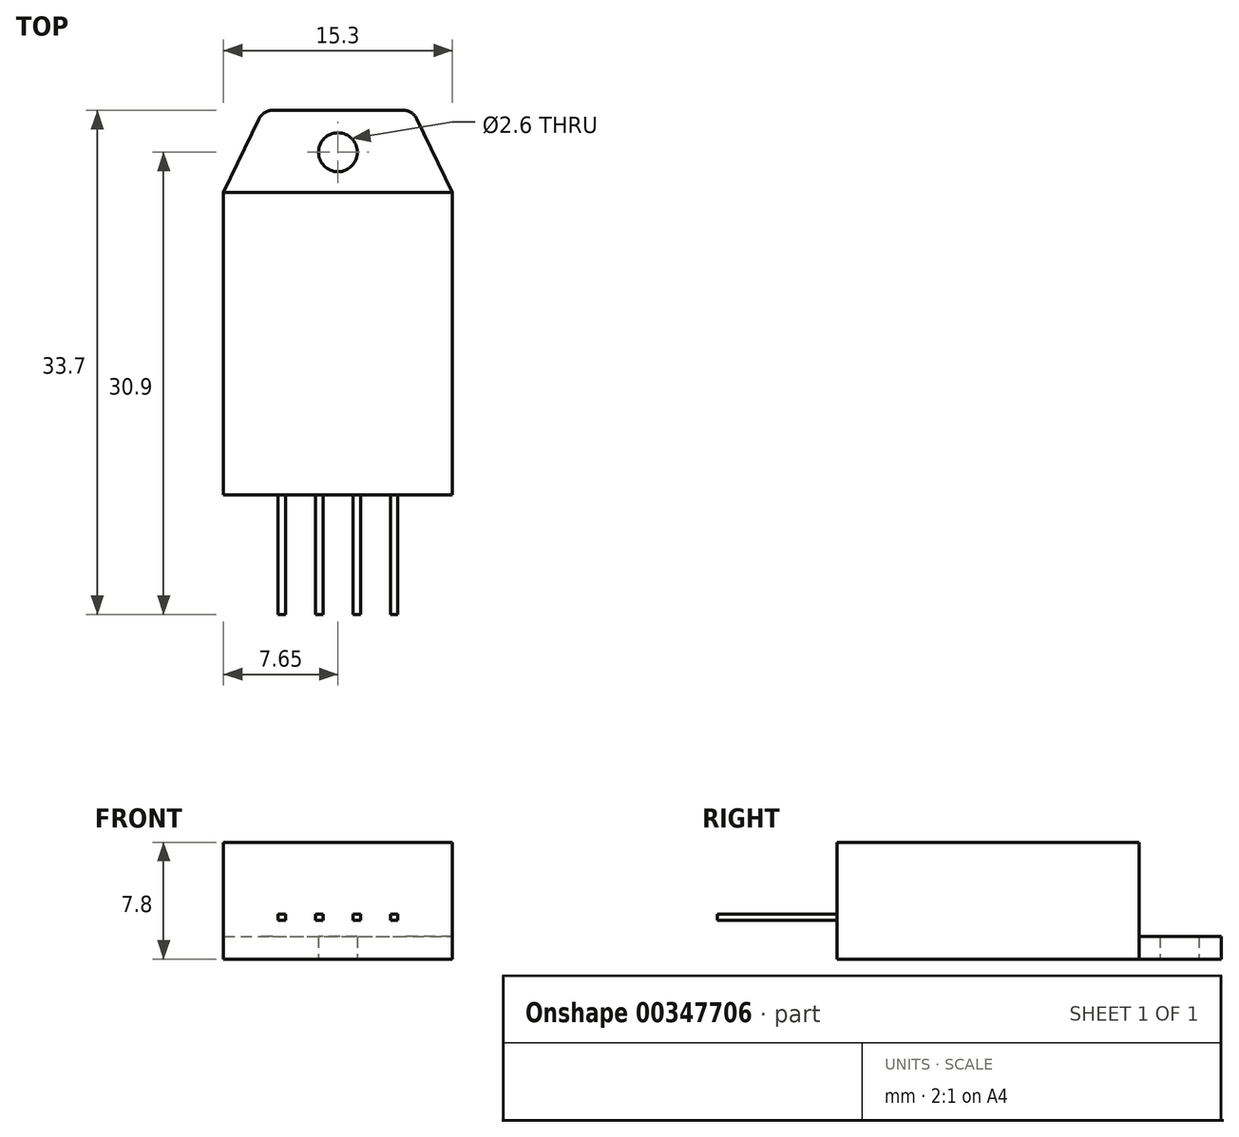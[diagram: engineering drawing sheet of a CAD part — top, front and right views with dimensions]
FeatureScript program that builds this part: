
annotation { "Feature Type Name" : "Feature", "Feature Type Description" : "" }
export const myFeature = defineFeature(function(context is Context, id is Id, definition is map)
    precondition{}
    {
        {
            var Q0;
            Q0=qCreatedBy(makeId("Top.planeOp"),FACE);
            var sketch = newSketch(context, id + "F0", { "sketchPlane" : qUnion([Q0])});
            skCircle(sketch, "E0", {"center": v(0, 0) * mm, "radius": 1.3 * mm});
            skLineSegment(sketch, "E1", {"start": v(-7.65, -22.9) * mm, "end": v(-7.65, -2.7) * mm});
            skLineSegment(sketch, "E2", {"start": v(-7.65, -2.7) * mm, "end": v(-5.27, 2.23) * mm});
            skLineSegment(sketch, "E3.MirrorCS", {"start": v(7.65, -2.7) * mm, "end": v(5.27, 2.23) * mm});
            skLineSegment(sketch, "E4.MirrorCS", {"start": v(7.65, -22.9) * mm, "end": v(7.65, -2.7) * mm});
            skLineSegment(sketch, "E5", {"start": v(-4.37, 2.8) * mm, "end": v(4.37, 2.8) * mm});
            skLineSegment(sketch, "E6", {"start": v(-7.65, -22.9) * mm, "end": v(7.65, -22.9) * mm});
            skLineSegment(sketch, "E7", {"start": v(-7.65, -2.7) * mm, "end": v(7.65, -2.7) * mm});
            skPoint(sketch, "E8.visualSharp", {"position": v(-5, 2.8) * mm});
            skArc(sketch, "E8.filletArc", {"start": v(-4.37, 2.8) * mm, "mid": v(-4.9, 2.65) * mm, "end": v(-5.27, 2.23) * mm});
            skPoint(sketch, "E9.visualSharp", {"position": v(5, 2.8) * mm});
            skArc(sketch, "E9.filletArc", {"start": v(5.27, 2.23) * mm, "mid": v(4.9, 2.65) * mm, "end": v(4.37, 2.8) * mm});
            skSolve(sketch);
        }
        {
            var Q0;
            Q0=makeQuery(id+"F0.imprint","IMPRINT",FACE,{"disambiguationData":[TD([[makeQuery(id+"F0.imprint","IMPRINT",EDGE,{"derivedFrom":sQuery(id+"F0.wireOp",EDGE,"E0")}),-1.0]])]});
            extrude(context, id + "F1", {"entities" : qUnion([Q0]), "depth" : 1.5 * mm});
        }
        {
            var Q0;
            Q0=makeQuery(id+"F0.imprint","IMPRINT",FACE,{"disambiguationData":[TD([[makeQuery(id+"F0.imprint","IMPRINT",EDGE,{"derivedFrom":sQuery(id+"F0.wireOp",EDGE,"E1")}),-1.0]])]});
            extrude(context, id + "F2", {"entities" : qUnion([Q0]), "operationType" : NewBodyOperationType.ADD, "depth" : 7.8 * mm});
        }
        {
            var Q0;
            Q0=makeQuery(id+"F2.opExtrude","SWEPT_FACE",FACE,{"disambiguationData":[OSD([sQuery(id+"F0.wireOp",EDGE,"E6")])]});
            var sketch = newSketch(context, id + "F3", { "sketchPlane" : qUnion([Q0])});
            skLineSegment(sketch, "E10.bottom", {"start": v(-4, 3) * mm, "end": v(-3.5, 3) * mm});
            skLineSegment(sketch, "E10.top", {"start": v(-4, 2.6) * mm, "end": v(-3.5, 2.6) * mm});
            skLineSegment(sketch, "E10.left", {"start": v(-4, 3) * mm, "end": v(-4, 2.6) * mm});
            skLineSegment(sketch, "E10.right", {"start": v(-3.5, 3) * mm, "end": v(-3.5, 2.6) * mm});
            skLineSegment(sketch, "E11.1.0.0", {"start": v(-1, 3) * mm, "end": v(-1, 2.6) * mm});
            skLineSegment(sketch, "E11.1.0.1", {"start": v(-1.5, 3) * mm, "end": v(-1.5, 2.6) * mm});
            skLineSegment(sketch, "E11.1.0.2", {"start": v(-1.5, 2.6) * mm, "end": v(-1, 2.6) * mm});
            skLineSegment(sketch, "E11.1.0.3", {"start": v(-1.5, 3) * mm, "end": v(-1, 3) * mm});
            skLineSegment(sketch, "E11.2.0.0", {"start": v(1.5, 3) * mm, "end": v(1.5, 2.6) * mm});
            skLineSegment(sketch, "E11.2.0.1", {"start": v(1, 3) * mm, "end": v(1, 2.6) * mm});
            skLineSegment(sketch, "E11.2.0.2", {"start": v(1, 2.6) * mm, "end": v(1.5, 2.6) * mm});
            skLineSegment(sketch, "E11.2.0.3", {"start": v(1, 3) * mm, "end": v(1.5, 3) * mm});
            skLineSegment(sketch, "E11.3.0.0", {"start": v(4, 3) * mm, "end": v(4, 2.6) * mm});
            skLineSegment(sketch, "E11.3.0.1", {"start": v(3.5, 3) * mm, "end": v(3.5, 2.6) * mm});
            skLineSegment(sketch, "E11.3.0.2", {"start": v(3.5, 2.6) * mm, "end": v(4, 2.6) * mm});
            skLineSegment(sketch, "E11.3.0.3", {"start": v(3.5, 3) * mm, "end": v(4, 3) * mm});
            skLineSegment(sketch, "E11.direction1", {"start": v(-4, 2.6) * mm, "end": v(-1.5, 2.6) * mm, "construction": true});
            skSolve(sketch);
        }
        {
            var Q0;
            Q0 = qSketchRegion(id + "F3", true);
            extrude(context, id + "F4", {"entities" : qUnion([Q0]), "operationType" : NewBodyOperationType.ADD, "depth" : 8 * mm});
        }
    });
